# Revit family: FP_Revit_18_OR36SCI6X1_Range_90001020A
name_source: partatom
category: Specialty Equipment
revit_build: Autodesk Revit 2018 (Build: 20170223_1515(x64)
units: mm (PartAtom-declared; Revit-internal decimal feet)

## family parameters
Always vertical = Yes
Cut with Voids When Loaded = Yes
OmniClass Number = 23.40.40.14.17.17
OmniClass Title = Ranges
Part Type = Normal
Room Calculation Point = No
Round Connector Dimension = Use Diameter
Shared = No
Work Plane-Based = No

## types (4) — shared parameters
Cavity - Depth = 641 mm  [stored 2.10302 ft]
Cavity - Width = 914 mm  [stored 2.99869 ft]
Chassis - Depth = 639 mm  [stored 2.09646 ft]
Chassis - Height = 814 mm
Chassis - Width = 911 mm  [stored 2.98885 ft]
Clearance - Overhead Combustible = 762 mm  [stored 2.5 ft]
Clearance - Overhead Non-Combustible = 610 mm  [stored 2.00131 ft]
Clearance - Overhead Rangehood = 610 mm  [stored 2.00131 ft]
Clearance - Rear Combustible = 50 mm  [stored 0.164042 ft]
Clearance - Side Combustible = 50 mm  [stored 0.164042 ft]
Connector Description - Electrical = 120/208 V or 120/240 V, 60 Hz, 40 A, *NEC Calculated load (50 A, Fused electrical supply)
Countertop Height (min 908mm - max 933mm) = 915 mm  [stored 3.00197 ft]
Manufacturer = Fisher & Paykel Appliances
Material - Body = Fisher & Paykel - Stainless Steel
Material - Buttons and Dials = Fisher & Paykel - Steel, Chrome Plated
Material - Cooktop = Fisher & Paykel - Black
Material - Door Front = Fisher & Paykel - Glass, Black
Material - Handle = Fisher & Paykel - Stainless Steel
Material - Trim = Fisher & Paykel - Steel, Chrome Plated
Optional - Rear Trim = TKOR366X1
Product - Depth = 693 mm
Product - Height = 915 mm  [stored 3.00197 ft]
Product - Width = 911 mm  [stored 2.98885 ft]
URL = www.fisherpaykel.com
Visibility - Adjustable Feet Covers = Yes
Visibility - Clearance Required = Yes
Visibility - Rear Trim (Supplied) = Yes
Visibility - Rear Trim 3"/76mm (Optional) = No
Visibility - Toe Kick Panel (Optional) = Yes
zero-valued in all types: Cavity - Height, Clearance - Rear Non-Combustible, Clearance - Side Non-Combustible

## per-type parameters (varying)
| type | Description | Material - COLOUR CHANGE | Model | Optional - Toe Kick Panel |
| OR36SCI6B (Black) | 36" Classic Freestanding Induction Range (Black) | Fisher & Paykel - Black | OR36SCI6B1 | KICKOR36B1 |
| OR36SCI6W (White) | 36" Classic Freestanding Induction Range (White) | Fisher & Paykel - White | OR36SCI6W1 | KICKOR36W1 |
| OR36SCI6R (Red) | 36" Classic Freestanding induction Range (Red) | Fisher & Paykel - Red | OR36SCI6R1 | KICKOR36R1 |
| OR36SCI6X (Stainless) | 36" Classic Freestanding Induction Range (Stainless) | Fisher & Paykel - Stainless Steel | OR36SCI6X1 | KICKOR36X1 |

note: [stored X ft] marks values corroborated as IEEE doubles in the binary element streams (Revit-internal decimal feet)

## geometry (parser evidence)
native form markers: Sweep x7
no freeform markers — native parametric forms only
